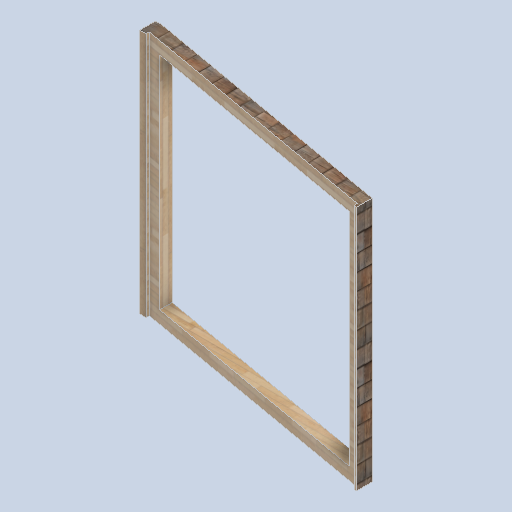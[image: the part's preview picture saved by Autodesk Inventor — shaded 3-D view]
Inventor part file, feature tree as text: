
AUTODESK INVENTOR PART (.ipt)
format: ipt  version: 2024.2 (Build 282272000, 272)  size: 184,320 bytes
history: native  units: in
note: dims shown in document units (in); Inventor stores cm internally (conversion verified against a paired STEP export)
features: plane x4, other x3, sketch x3
ambient origin geometry x8: Origin, YZ Plane, XZ Plane, XY Plane, X Axis, Y Axis, Z Axis, Center Point
bodies: Solid1 (feature_tree)
feature tree (10):
  other  "eave_frame_side_.ipt"
  other  "Solid1::eave_frame_side_.ipt"
  other  "TaggingFeature1"
  sketch  "Sketch1"  dims[d0=0.3937in]
  sketch  "Sketch6"
  sketch  "Sketch11"
  plane  "Work Plane1"
  plane  "Work Plane2"
  plane  "Work Plane3"
  plane  "Work Plane4"
